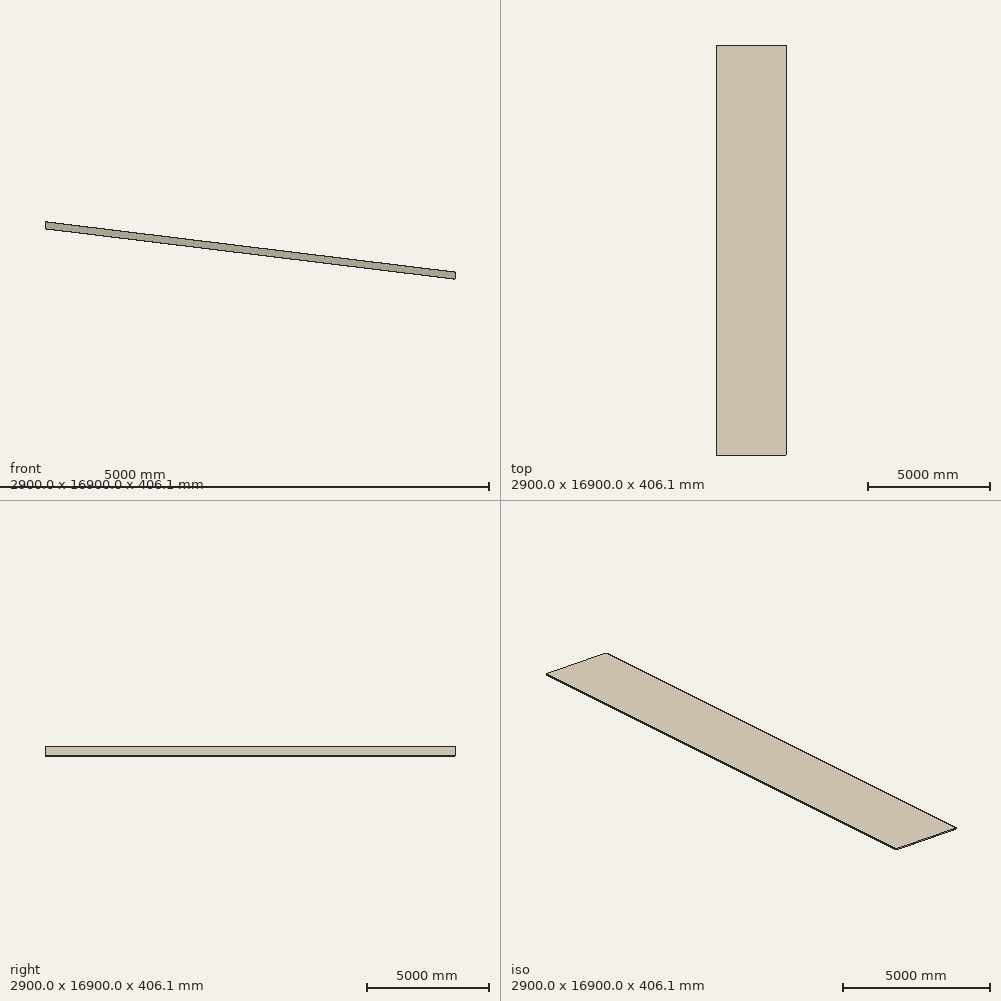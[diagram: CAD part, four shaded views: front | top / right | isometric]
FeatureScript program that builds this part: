
annotation { "Feature Type Name" : "Feature", "Feature Type Description" : "" }
export const myFeature = defineFeature(function(context is Context, id is Id, definition is map)
    precondition{}
    {
        {
            var Q0;
            Q0=qCreatedBy(makeId("Front.planeOp"),FACE);
            var sketch = newSketch(context, id + "F0", { "sketchPlane" : qUnion([Q0])});
            skLineSegment(sketch, "E0", {"start": v(0, 0) * mm, "end": v(-2900, 356.08) * mm});
            skLineSegment(sketch, "E1", {"start": v(-2900, 356.08) * mm, "end": v(-2900, 406.08) * mm});
            skLineSegment(sketch, "E2", {"start": v(-2900, 406.08) * mm, "end": v(0, 50) * mm});
            skLineSegment(sketch, "E3", {"start": v(0, 50) * mm, "end": v(0, 0) * mm});
            skSolve(sketch);
        }
        {
            var Q0;
            Q0=makeQuery(id+"F0.imprint","IMPRINT",FACE,{"disambiguationData":[TD([[makeQuery(id+"F0.imprint","IMPRINT",EDGE,{"derivedFrom":sQuery(id+"F0.wireOp",EDGE,"E0")}),-1.0]])]});
            extrude(context, id + "F1", {"entities" : qUnion([Q0]), "depth" : 16900 * mm});
        }
    });
